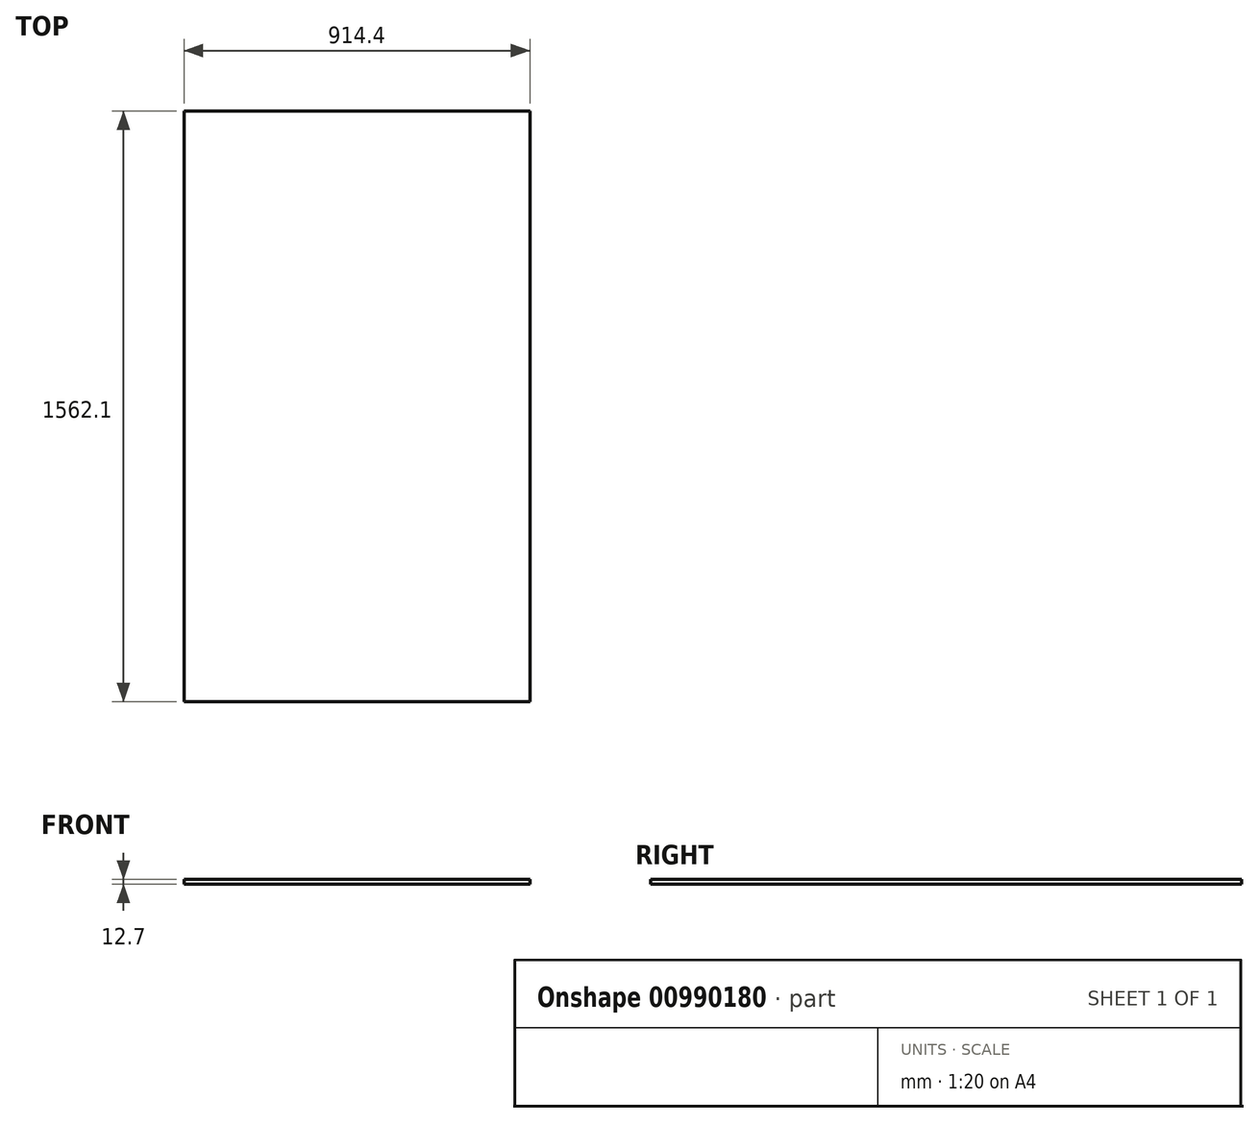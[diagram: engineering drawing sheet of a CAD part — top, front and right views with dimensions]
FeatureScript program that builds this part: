
annotation { "Feature Type Name" : "Feature", "Feature Type Description" : "" }
export const myFeature = defineFeature(function(context is Context, id is Id, definition is map)
    precondition{}
    {
        {
            var Q0;
            Q0=qCreatedBy(makeId("Top.planeOp"),FACE);
            var sketch = newSketch(context, id + "F0", { "sketchPlane" : qUnion([Q0])});
            skLineSegment(sketch, "E0.bottom", {"start": v(457.2, 781.05) * mm, "end": v(-457.2, 781.05) * mm});
            skLineSegment(sketch, "E0.top", {"start": v(457.2, -781.05) * mm, "end": v(-457.2, -781.05) * mm});
            skLineSegment(sketch, "E0.left", {"start": v(457.2, 781.05) * mm, "end": v(457.2, -781.05) * mm});
            skLineSegment(sketch, "E0.right", {"start": v(-457.2, 781.05) * mm, "end": v(-457.2, -781.05) * mm});
            skPoint(sketch, "E0.middle", {"position": v(0, 0) * mm});
            skSolve(sketch);
        }
        {
            var Q0;
            Q0=qSketchRegion(id+"F0",true);
            extrude(context, id + "F1", {"entities" : qUnion([Q0]), "depth" : 12.7 * mm, "offsetDistance" : 25.4 * mm});
        }
    });
